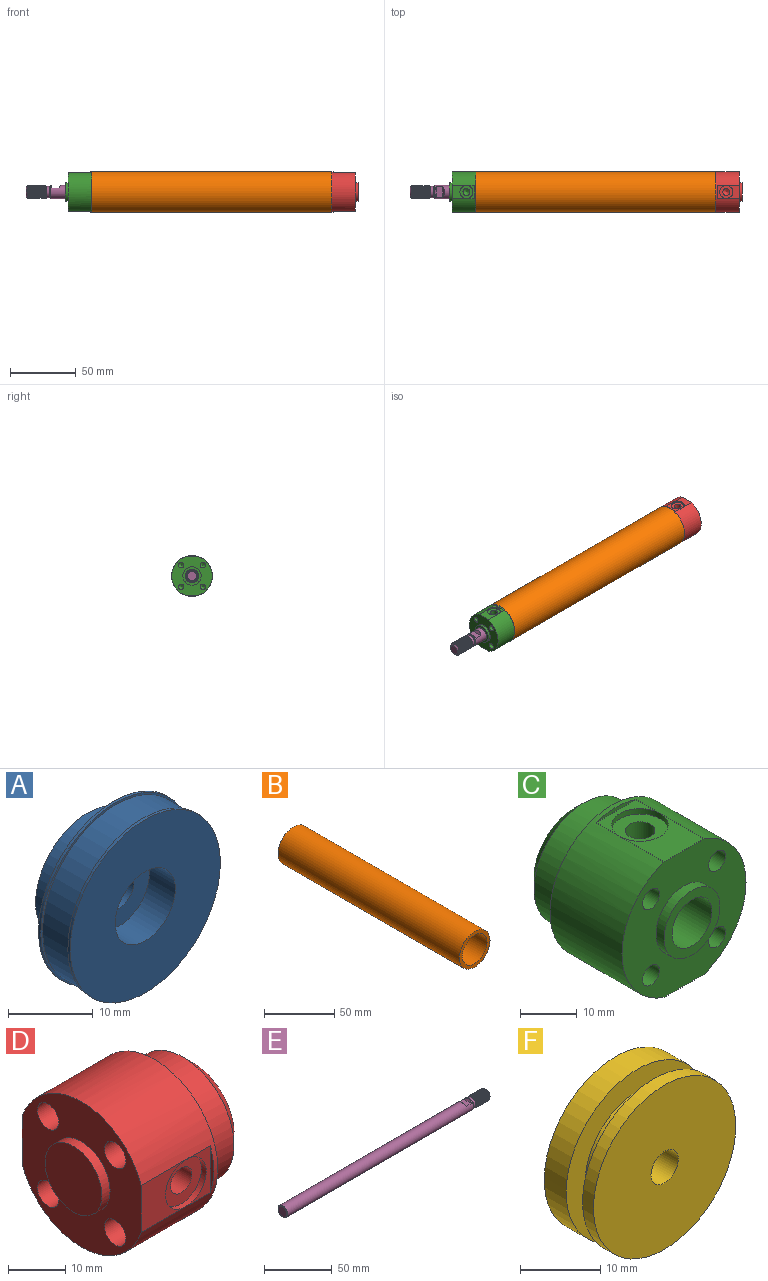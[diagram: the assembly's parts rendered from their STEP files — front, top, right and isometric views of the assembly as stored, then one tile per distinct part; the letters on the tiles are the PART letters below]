
ASSEMBLY  parts=6 mates=6
PART A: 12 faces, bbox 25x9.6x25 mm
  f0: cylinder r=12.5mm len=25mm, axis (0,1,0), area 30.6mm2, adj f1,f6
  f1: plane 25x25mm, normal (0,-1,0), area 412.3mm2, adj f0,f2
  f2: cylinder r=5mm len=10mm, axis (0,-1,0), area 135.7mm2, adj f1,f3
  f3: plane 10x10mm, normal (0,-1,0), area 60.4mm2, adj f2,f11
  f4: cylinder r=12.2mm len=24.4mm, axis (0,1,0), area 344.9mm2, adj f5,f6
  f5: plane 25x25mm, normal (0,-1,0), area 23.3mm2, adj f4,f10
  f6: plane 25x25mm, normal (0,1,0), area 23.3mm2, adj f0,f4
  f7: plane 17.3x17.3mm, normal (0,1,0), area 217mm2, adj f8,f11
  f8: cylinder r=8.65mm len=17.3mm, axis (0,-1,0), area 234.8mm2, adj f7,f9
  f9: plane 25x25mm, normal (0,1,0), area 255.8mm2, adj f8,f10
  f10: cylinder r=12.5mm len=25mm, axis (0,1,0), area 30.6mm2, adj f5,f9
  f11: cylinder r=2.4mm len=5.28mm, axis (0,-1,0), area 79.6mm2, adj f3,f7
PART B: 4 faces, bbox 31x183x31 mm
  f0: cylinder r=12.5mm len=183mm, axis (0,1,0), area 14372.8mm2, adj f2,f3
  f1: cylinder r=15.5mm len=183mm, axis (0,1,0), area 17822.3mm2, adj f2,f3
  f2: plane 31x31mm, normal (0,-1,0), area 263.9mm2, adj f0,f1
  f3: plane 31x31mm, normal (0,1,0), area 263.9mm2, adj f0,f1
PART C: 31 faces, bbox 31x29.5x31 mm
  f0: cylinder r=15.5mm len=31mm, axis (0,1,0), area 1406.8mm2, adj f1,f3,f17,f18,f19,f20,f21,f22
  f1: plane 31x29.34mm, normal (0,-1,0), area 534.3mm2, adj f0,f4,f6,f8,f10,f12,f17,f22
  f2: cylinder r=5mm len=29.5mm, axis (0,1,0), area 926.8mm2, adj f5,f15
  f3: plane 31x31mm, normal (0,1,0), area 263.9mm2, adj f0,f14
  f4: cylinder r=7mm len=14mm, axis (0,1,0), area 88mm2, adj f1,f5
  f5: plane 14x14mm, normal (0,-1,0), area 75.4mm2, adj f2,f4
  f6: cylinder r=2.1mm len=9.9mm, axis (0,-1,0), area 130.6mm2, adj f1,f7
  f7: cone r=0mm half-angle=59deg, axis (0,-1,0), area 16.2mm2, adj f6
  f8: cylinder r=2.1mm len=9.9mm, axis (0,-1,0), area 130.6mm2, adj f1,f9
  f9: cone r=0mm half-angle=59deg, axis (0,-1,0), area 16.2mm2, adj f8
  f10: cylinder r=2.1mm len=9.9mm, axis (0,-1,0), area 130.6mm2, adj f1,f11
  f11: cone r=0mm half-angle=59deg, axis (0,-1,0), area 16.2mm2, adj f10
  f12: cylinder r=2.1mm len=9.9mm, axis (0,-1,0), area 130.6mm2, adj f1,f13
  f13: cone r=0mm half-angle=59deg, axis (0,-1,0), area 16.2mm2, adj f12
  f14: cylinder r=12.5mm len=25mm, axis (0,-1,0), area 549.8mm2, adj f3,f16
  f15: plane 20x20mm, normal (0,1,0), area 235.6mm2, adj f2,f16
  f16: cone r=10mm half-angle=45deg, axis (0,-1,0), area 249.9mm2, adj f14,f15
  f17: plane 11x10mm, normal (0,0,-1), area 70.7mm2, adj f0,f1,f26
  f18: plane 10x6mm, normal (0,0,-1), area 20.7mm2, adj f0,f19,f26
  f19: plane 10x0.83mm, normal (0,-1,0), area 5.6mm2, adj f0,f18
  f20: plane 10x6mm, normal (0,0,1), area 20.7mm2, adj f0,f21,f30
  f21: plane 10x0.83mm, normal (0,-1,0), area 5.6mm2, adj f0,f20
  f22: plane 11x10mm, normal (0,0,1), area 70.7mm2, adj f0,f1,f30
  f23: cone r=0mm half-angle=59deg, axis (0,0,-1), area 25.3mm2, adj f24
  f24: cylinder r=2.62mm len=6.25mm, axis (0,0,-1), area 103.1mm2, adj f23,f25
  f25: plane 10x10mm, normal (0,0,-1), area 56.9mm2, adj f24,f26
  f26: cylinder r=5mm len=10mm, axis (0,0,-1), area 36.8mm2, adj f17,f18,f25
  f27: cone r=0mm half-angle=59deg, axis (0,0,1), area 25.3mm2, adj f28
  f28: cylinder r=2.62mm len=6.25mm, axis (0,0,1), area 103.1mm2, adj f27,f29
  f29: plane 10x10mm, normal (0,0,1), area 56.9mm2, adj f28,f30
  f30: cylinder r=5mm len=10mm, axis (0,0,1), area 36.8mm2, adj f20,f22,f29
PART D: 30 faces, bbox 29.5x31x31 mm
  f0: cylinder r=15.5mm len=31mm, axis (1,0,0), area 1406.8mm2, adj f1,f3,f16,f17,f18,f19,f20,f21
  f1: plane 31x29.34mm, normal (-1,0,0), area 503.1mm2, adj f0,f4,f5,f7,f9,f11,f16,f21
  f2: plane 14x14mm, normal (-1,0,0), area 153.9mm2, adj f4
  f3: plane 31x31mm, normal (1,0,0), area 263.9mm2, adj f0,f13
  f4: cylinder r=7mm len=14mm, axis (1,0,0), area 88mm2, adj f1,f2
  f5: cylinder r=2.62mm len=7mm, axis (-1,0,0), area 115.5mm2, adj f1,f6
  f6: cone r=0mm half-angle=59deg, axis (-1,0,0), area 25.3mm2, adj f5
  f7: cylinder r=2.62mm len=7mm, axis (-1,0,0), area 115.5mm2, adj f1,f8
  f8: cone r=0mm half-angle=59deg, axis (-1,0,0), area 25.3mm2, adj f7
  f9: cylinder r=2.62mm len=7mm, axis (-1,0,0), area 115.5mm2, adj f1,f10
  f10: cone r=0mm half-angle=59deg, axis (-1,0,0), area 25.3mm2, adj f9
  f11: cylinder r=2.62mm len=7mm, axis (-1,0,0), area 115.5mm2, adj f1,f12
  f12: cone r=0mm half-angle=59deg, axis (-1,0,0), area 25.3mm2, adj f11
  f13: cylinder r=12.5mm len=25mm, axis (-1,0,0), area 549.8mm2, adj f3,f15
  f14: plane 20x20mm, normal (1,0,0), area 314.2mm2, adj f15
  f15: cone r=10mm half-angle=45deg, axis (-1,0,0), area 249.9mm2, adj f13,f14
  f16: plane 10x10mm, normal (0,1,0), area 60.7mm2, adj f0,f1,f25
  f17: plane 10x7mm, normal (0,1,0), area 30.7mm2, adj f0,f18,f25
  f18: plane 10x0.83mm, normal (-1,0,0), area 5.6mm2, adj f0,f17
  f19: plane 10x6mm, normal (0,-1,0), area 20.7mm2, adj f0,f20,f29
  f20: plane 10x0.83mm, normal (-1,0,0), area 5.6mm2, adj f0,f19
  f21: plane 11x10mm, normal (0,-1,0), area 70.7mm2, adj f0,f1,f29
  f22: cone r=0mm half-angle=59deg, axis (0,1,0), area 25.3mm2, adj f23
  f23: cylinder r=2.62mm len=6.25mm, axis (0,1,0), area 103.1mm2, adj f22,f24
  f24: plane 10x10mm, normal (0,1,0), area 56.9mm2, adj f23,f25
  f25: cylinder r=5mm len=10mm, axis (0,1,0), area 36.8mm2, adj f16,f17,f24
  f26: cone r=0mm half-angle=59deg, axis (0,-1,0), area 25.3mm2, adj f27
  f27: cylinder r=2.62mm len=6.25mm, axis (0,-1,0), area 103.1mm2, adj f26,f28
  f28: plane 10x10mm, normal (0,-1,0), area 56.9mm2, adj f27,f29
  f29: cylinder r=5mm len=10mm, axis (0,-1,0), area 36.8mm2, adj f19,f21,f28
PART E: 19 faces, bbox 213.4x10x11.5 mm
  f0: plane 9x9mm, normal (-1,0,0), area 6.9mm2, adj f4,f16
  f1: cylinder r=5mm len=194.43mm, axis (1,0,0), area 6047.8mm2, adj f7,f8,f9,f14,f15,f17,f18
  f2: plane 7x7mm, normal (1,0,0), area 38.5mm2, adj f13
  f3: cylinder r=5mm len=13.5mm, axis (1,0,0), area 3.1mm2, adj f10,f11,f12,f13,f16
  f4: cylinder r=4.25mm len=8.5mm, axis (1,0,0), area 66.8mm2, adj f0,f5
  f5: plane 9x9mm, normal (1,0,0), area 6.9mm2, adj f4,f17
  f6: plane 9x9mm, normal (-1,0,0), area 63.6mm2, adj f18
  f7: plane 8x0mm, normal (1,0,0), area 0mm2, adj f1,f9,f15
  f8: plane 8x0mm, normal (-1,0,0), area 0mm2, adj f1,f9,f14
  f9: plane 8x5mm, normal (0,0,1), area 40mm2, adj f1,f7,f8
  f10: bspline ~15.12x11.55mm, area 359.9mm2, adj f3,f11,f12,f13
  f11: plane 0.78x0.63mm, normal (0,0,-1), area 0.2mm2, adj f3,f10,f12,f16
  f12: bspline ~15.12x11.55mm, area 369.5mm2, adj f3,f10,f11,f13,f16
  f13: cone r=3.5mm half-angle=45deg, axis (-1,0,0), area 41.9mm2, adj f2,f3,f10,f12
  f14: plane 7.99x2mm, normal (-0.87,0,0.5), area 12.9mm2, adj f1,f8
  f15: plane 7.99x2mm, normal (0.87,0,0.5), area 12.9mm2, adj f1,f7
  f16: cone r=5mm half-angle=45deg, axis (1,0,0), area 13.4mm2, adj f0,f3,f11,f12
  f17: cone r=4.5mm half-angle=45deg, axis (-1,0,0), area 21.1mm2, adj f1,f5
  f18: cone r=5mm half-angle=45deg, axis (1,0,0), area 21.1mm2, adj f1,f6
PART F: 10 faces, bbox 25x8.7x25 mm
  f0: cylinder r=2.4mm len=4.8mm, axis (0,-1,0), area 72.4mm2, adj f1,f9
  f1: plane 17.3x17.3mm, normal (0,1,0), area 217mm2, adj f0,f2
  f2: cylinder r=8.65mm len=17.3mm, axis (0,-1,0), area 209.2mm2, adj f1,f3
  f3: plane 25x25mm, normal (0,1,0), area 255.8mm2, adj f2,f4
  f4: cylinder r=12.5mm len=25mm, axis (0,-1,0), area 302.4mm2, adj f3,f5
  f5: plane 25x25mm, normal (0,-1,0), area 228.4mm2, adj f4,f6
  f6: cylinder r=9.14mm len=18.28mm, axis (0,-1,0), area 165.4mm2, adj f5,f7
  f7: plane 25x25mm, normal (0,1,0), area 228.4mm2, adj f6,f8
  f8: cylinder r=12.5mm len=25mm, axis (0,-1,0), area 150.8mm2, adj f7,f9
  f9: plane 25x25mm, normal (0,-1,0), area 472.8mm2, adj f0,f8
PLACE A rot(axis=(0,0,-1),90deg) t=(296.27,-43.49,-201.99)mm
PLACE B rot(axis=(0,0,1),90deg) t=(131.89,-43.49,-201.99)mm
PLACE C rot(axis=(0.71,0.71,0),180deg) t=(131.89,-43.49,-201.99)mm
PLACE D rot(axis=(0,-0.71,-0.71),180deg) t=(314.89,-43.49,-201.99)mm
PLACE E rot(axis=(0,0,-1),180deg) t=(295.31,-43.49,-201.99)mm
PLACE F rot(axis=(0.71,-0.71,0),180deg) t=(305.39,-43.49,-201.99)mm
MATE slider B.f0 <-> F.f0  axis (1,0,0) through (314.89,-43.49,-201.99)mm
MATE fastened E.f1 <-> A.f0  axis (1,0,0) through (295.31,-43.49,-201.99)mm
MATE fastened D.f13 <-> B.f0  axis (1,0,0) through (314.89,-43.49,-201.99)mm
MATE fastened A.f0 <-> F.f0  axis (1,0,0) through (300.59,-43.49,-201.99)mm
MATE planar C.f0 <-> B.f0  axis (-1,0,0) through (131.89,-43.49,-201.99)mm
MATE fastened C.f0 <-> B.f0  axis (1,0,0) through (131.89,-43.49,-201.99)mm
